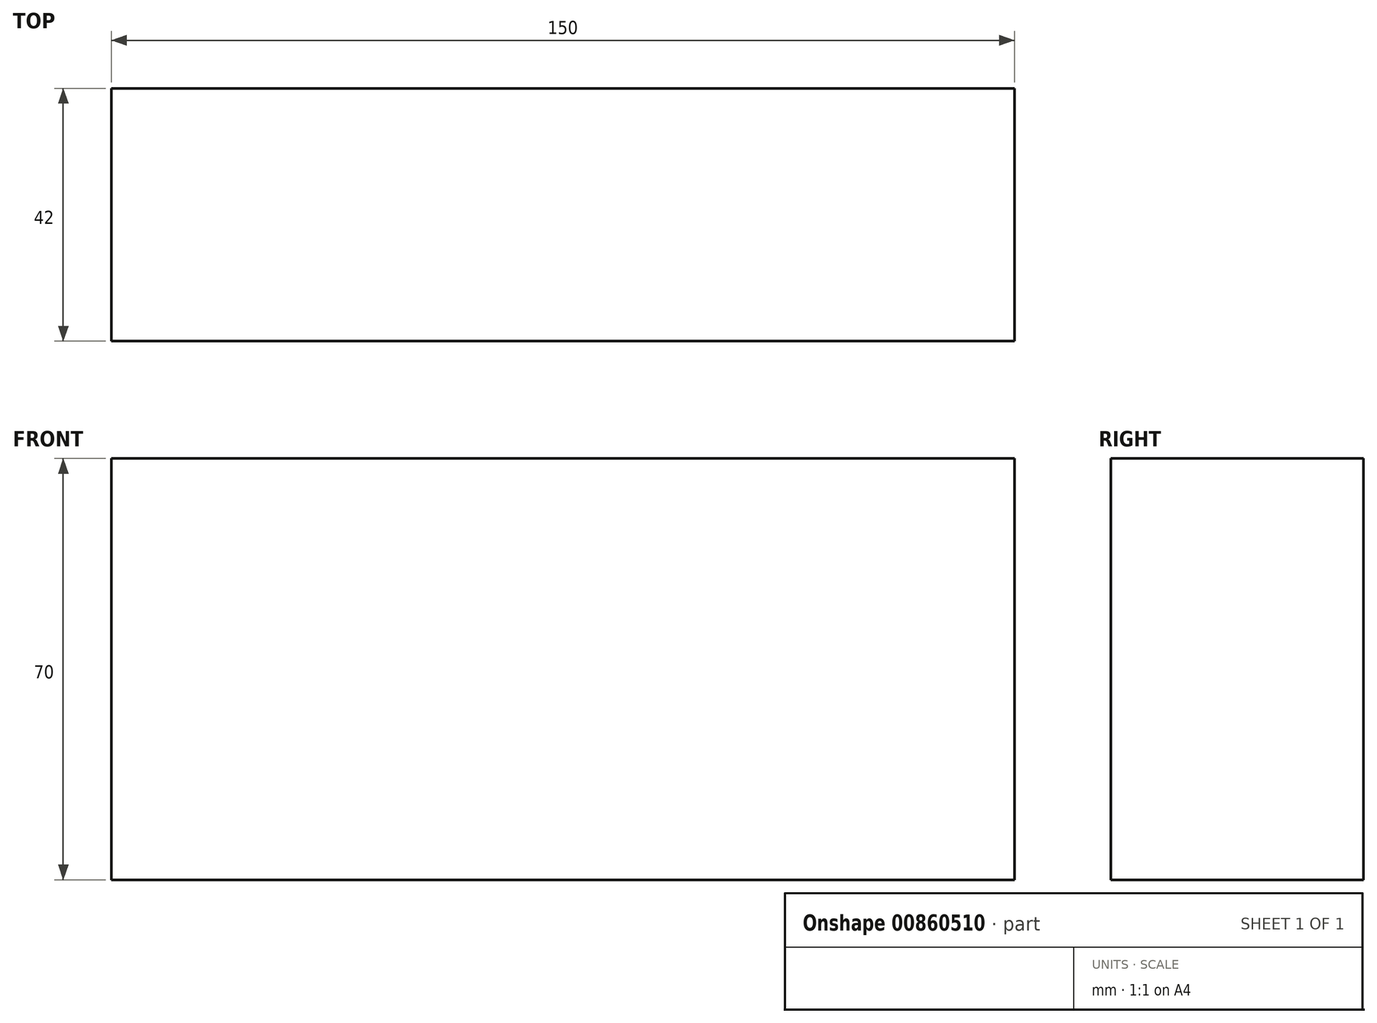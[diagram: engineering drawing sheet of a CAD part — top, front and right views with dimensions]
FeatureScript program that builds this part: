
annotation { "Feature Type Name" : "Feature", "Feature Type Description" : "" }
export const myFeature = defineFeature(function(context is Context, id is Id, definition is map)
    precondition{}
    {
        {
            var Q0;
            Q0=qCreatedBy(makeId("Front.planeOp"),FACE);
            var sketch = newSketch(context, id + "F0", { "sketchPlane" : qUnion([Q0])});
            skLineSegment(sketch, "E0.bottom", {"start": v(-50.33, 47.26) * mm, "end": v(99.67, 47.26) * mm});
            skLineSegment(sketch, "E0.top", {"start": v(-50.33, -22.74) * mm, "end": v(99.67, -22.74) * mm});
            skLineSegment(sketch, "E0.left", {"start": v(-50.33, 47.26) * mm, "end": v(-50.33, -22.74) * mm});
            skLineSegment(sketch, "E0.right", {"start": v(99.67, 47.26) * mm, "end": v(99.67, -22.74) * mm});
            skSolve(sketch);
        }
        {
            var Q0;
            Q0=makeQuery(id+"F0.imprint","IMPRINT",FACE,{"disambiguationData":[TD([[makeQuery(id+"F0.imprint","IMPRINT",EDGE,{"derivedFrom":sQuery(id+"F0.wireOp",EDGE,"E0.bottom")}),-1.0]])]});
            extrude(context, id + "F1", {"entities" : qUnion([Q0]), "depth" : 42 * mm, "offsetDistance" : 25 * mm});
        }
        {
            var Q0;
            Q0=makeQuery(id+"F1.opExtrude","CAP_FACE",FACE,{"disambiguationData":[OSD([sQuery(id+"F0.wireOp",EDGE,"E0.bottom"),sQuery(id+"F0.wireOp",EDGE,"E0.top"),sQuery(id+"F0.wireOp",EDGE,"E0.left"),sQuery(id+"F0.wireOp",EDGE,"E0.right")])],"isStart":false});
            var sketch = newSketch(context, id + "F2", { "sketchPlane" : qUnion([Q0])});
            skCircle(sketch, "E1", {"center": v(-18.87, 13.88) * mm, "radius": 13.9 * mm});
            skSolve(sketch);
        }
        {
            var Q0;
            Q0=makeQuery(id+"F2.imprint","IMPRINT",FACE,{"disambiguationData":[TD([[makeQuery(id+"F2.imprint","IMPRINT",EDGE,{"derivedFrom":sQuery(id+"F2.wireOp",EDGE,"E1")}),1.0]])]});
            extrude(context, id + "F3", {"entities" : qUnion([Q0]), "operationType" : NewBodyOperationType.ADD, "endBound" : BoundingType.UP_TO_NEXT, "oppositeDirection" : true, "depth" : 148 * mm, "offsetDistance" : 25 * mm});
        }
    });
